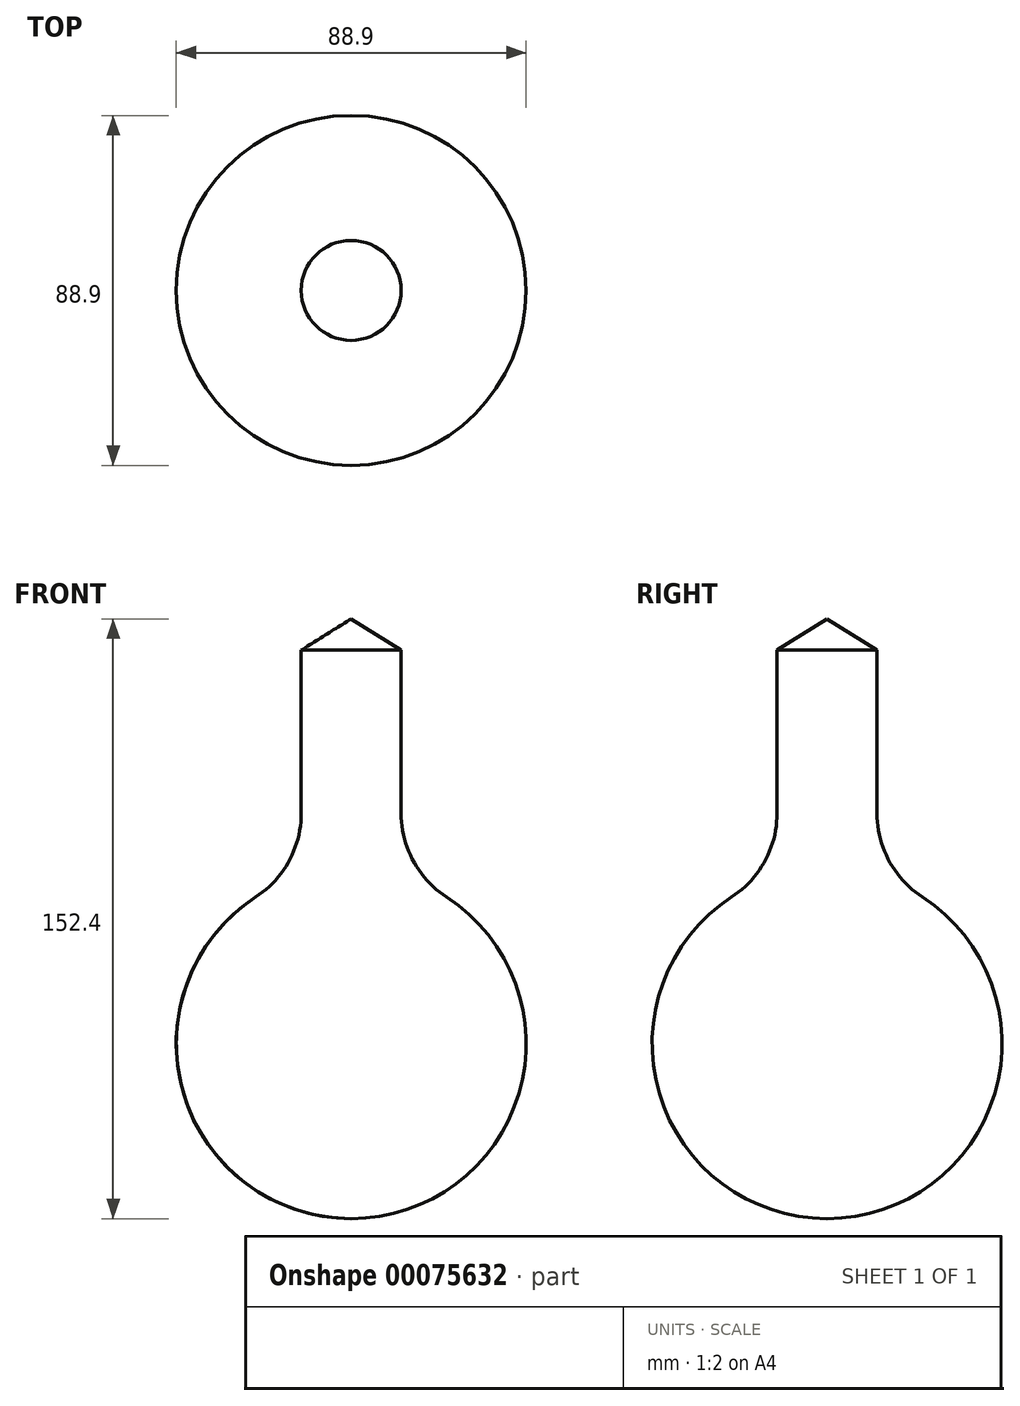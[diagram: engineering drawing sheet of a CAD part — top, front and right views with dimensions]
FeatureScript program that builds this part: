
annotation { "Feature Type Name" : "Feature", "Feature Type Description" : "" }
export const myFeature = defineFeature(function(context is Context, id is Id, definition is map)
    precondition{}
    {
        {
            var Q0;
            Q0=qCreatedBy(makeId("Front.planeOp"),FACE);
            var sketch = newSketch(context, id + "F0", { "sketchPlane" : qUnion([Q0])});
            skLineSegment(sketch, "E0", {"start": v(0, 0) * mm, "end": v(12.7, -7.96) * mm});
            skLineSegment(sketch, "E1", {"start": v(12.7, -7.96) * mm, "end": v(12.7, -49.4) * mm});
            skArc(sketch, "E2", {"start": v(0, -152.4) * mm, "mid": v(42.61, -120.6) * mm, "end": v(24.25, -70.7) * mm});
            skLineSegment(sketch, "E3", {"start": v(0, 0) * mm, "end": v(0, 40.68) * mm, "construction": true});
            skLineSegment(sketch, "E4", {"start": v(44.45, -64.8) * mm, "end": v(44.45, -130.37) * mm, "construction": true});
            skPoint(sketch, "E5.visualSharp", {"position": v(12.7, -65.35) * mm});
            skArc(sketch, "E5.filletArc", {"start": v(12.7, -49.4) * mm, "mid": v(15.77, -61.51) * mm, "end": v(24.25, -70.7) * mm});
            skLineSegment(sketch, "E6", {"start": v(0, 0) * mm, "end": v(0, -152.4) * mm});
            skSolve(sketch);
        }
        {
            var Q0;
            Q0 = qSketchRegion(id + "F0", true);
            var Q1;
            Q1=sQuery(id+"F0.wireOp",EDGE,"E3");
            revolve(context, id + "F1", {"entities" : qUnion([Q0]), "axis" : qUnion([Q1]), "revolveType" : RevolveType.FULL});
        }
    });
